# Revit family: vanity unit with 2 drawers
name_source: partatom
category: Furniture
units: mm (PartAtom-declared; Revit-internal decimal feet)

## family parameters
Always vertical = Yes
Cut with Voids When Loaded = No
OmniClass Number = 23.21.19.15.33.13
Room Calculation Point = No
Shared = Yes
Work Plane-Based = No

## types (120) — shared parameters
BIMOBJECT = Sanitary: Compound units
CATALOG = Hansgrohe
DESIGN = Germany
ETIM = EC011381 | Bathroom furniture set
IFC = Furnishing element
MASTERFORMAT = 12 35 30.23 | Bathroom Casework
Manufacturer = Hansgrohe
NBSYN = $BASENUMBER.-$ARTNR.-$OBERFLAECHE.-$SURFACE.-$LODLEVEL.
NN = Vanity Unit with 2 Drawers
OBJECTTYPE = Object (single object)
OMNICLASS = 23-21 19 15 33 13 | Residential Bathroom Specialty Casework
PRODUCTFAMILY = Xelu Q
PRODUCTGROUP = vanity unit
PRODUCTURL = https://pro.hansgrohe.com
REGIONSET = Worldwide
UNICLASS2015 = Pr_40_30_78_05 | Bathroom furniture
UNICLASS_2015_CODE = 40_30_78_05
UNIFORMATII = E2010 | Fixed Furnishings
UNSPSC = 56 | Furniture and Furnishings
etim7_EC011381 = EC011381

## per-type parameters (varying)
| type | ARTNR | BASENUMBER | GTINCODE | L | LINA | LODLEVEL | Model | NAME | NB | OBERFLAECHE | PERMALINK | SURFACE | WEIGHT |
| Vanity unit 1180_475 with 2 drawers for washbasin-54035000-High Gloss White-CHROME-200 | 54035000 | Vanity unit 1180/475 with 2 drawers for washbasin | 4059625455807 | 1180 | Vanity unit 1180/475 with 2 drawers for washbasin-54035000-High Gloss White-CHROME-200 | 200 | Vanity unit 1180/475 with 2 drawers for washbasin-54035000-High Gloss White-CHROME-200 | Xelu Q Vanity unit High Gloss White 1180/475 with 2 drawers for washbasin | Vanity unit 1180/475 with 2 drawers for washbasin-54035000-High Gloss White-CHROME-200 | High Gloss White | 54035XXX | CHROME | 45.5 |
| Vanity unit 1180_475 with 2 drawers for washbasin-54035000-High Gloss White-CHROME-400 | 54035000 | Vanity unit 1180/475 with 2 drawers for washbasin | 4059625455807 | 1180 | Vanity unit 1180/475 with 2 drawers for washbasin-54035000-High Gloss White-CHROME-400 | 400 | Vanity unit 1180/475 with 2 drawers for washbasin-54035000-High Gloss White-CHROME-400 | Xelu Q Vanity unit High Gloss White 1180/475 with 2 drawers for washbasin | Vanity unit 1180/475 with 2 drawers for washbasin-54035000-High Gloss White-CHROME-400 | High Gloss White | 54035XXX | CHROME | 45.5 |
| Vanity unit 1180_475 with 2 drawers for washbasin-54035670-High Gloss White-MATT_BLACK-200 | 54035670 | Vanity unit 1180/475 with 2 drawers for washbasin | 4059625455807 | 1180 | Vanity unit 1180/475 with 2 drawers for washbasin-54035670-High Gloss White-MATT_BLACK-200 | 200 | Vanity unit 1180/475 with 2 drawers for washbasin-54035670-High Gloss White-MATT_BLACK-200 | Xelu Q Vanity unit High Gloss White 1180/475 with 2 drawers for washbasin | Vanity unit 1180/475 with 2 drawers for washbasin-54035670-High Gloss White-MATT_BLACK-200 | High Gloss White | 54035XXX | MATT_BLACK | 45.5 |
| Vanity unit 1180_475 with 2 drawers for washbasin-54035670-High Gloss White-MATT_BLACK-400 | 54035670 | Vanity unit 1180/475 with 2 drawers for washbasin | 4059625455807 | 1180 | Vanity unit 1180/475 with 2 drawers for washbasin-54035670-High Gloss White-MATT_BLACK-400 | 400 | Vanity unit 1180/475 with 2 drawers for washbasin-54035670-High Gloss White-MATT_BLACK-400 | Xelu Q Vanity unit High Gloss White 1180/475 with 2 drawers for washbasin | Vanity unit 1180/475 with 2 drawers for washbasin-54035670-High Gloss White-MATT_BLACK-400 | High Gloss White | 54035XXX | MATT_BLACK | 45.5 |
| Vanity unit 1180_475 with 2 drawers for washbasin-54035700-High Gloss White-MATT_WHITE-200 | 54035700 | Vanity unit 1180/475 with 2 drawers for washbasin | 4059625455807 | 1180 | Vanity unit 1180/475 with 2 drawers for washbasin-54035700-High Gloss White-MATT_WHITE-200 | 200 | Vanity unit 1180/475 with 2 drawers for washbasin-54035700-High Gloss White-MATT_WHITE-200 | Xelu Q Vanity unit High Gloss White 1180/475 with 2 drawers for washbasin | Vanity unit 1180/475 with 2 drawers for washbasin-54035700-High Gloss White-MATT_WHITE-200 | High Gloss White | 54035XXX | MATT_WHITE | 45.5 |
| Vanity unit 1180_475 with 2 drawers for washbasin-54035700-High Gloss White-MATT_WHITE-400 | 54035700 | Vanity unit 1180/475 with 2 drawers for washbasin | 4059625455807 | 1180 | Vanity unit 1180/475 with 2 drawers for washbasin-54035700-High Gloss White-MATT_WHITE-400 | 400 | Vanity unit 1180/475 with 2 drawers for washbasin-54035700-High Gloss White-MATT_WHITE-400 | Xelu Q Vanity unit High Gloss White 1180/475 with 2 drawers for washbasin | Vanity unit 1180/475 with 2 drawers for washbasin-54035700-High Gloss White-MATT_WHITE-400 | High Gloss White | 54035XXX | MATT_WHITE | 45.5 |
| Vanity unit 1180_475 with 2 drawers for washbasin-54036000-Diamond Matt Grey-CHROME-200 | 54036000 | Vanity unit 1180/475 with 2 drawers for washbasin | 4059625455777 | 1180 | Vanity unit 1180/475 with 2 drawers for washbasin-54036000-Diamond Matt Grey-CHROME-200 | 200 | Vanity unit 1180/475 with 2 drawers for washbasin-54036000-Diamond Matt Grey-CHROME-200 | Xelu Q Vanity unit Diamond Matt Grey 1180/475 with 2 drawers for washbasin | Vanity unit 1180/475 with 2 drawers for washbasin-54036000-Diamond Matt Grey-CHROME-200 | Diamond Matt Grey | 54036XXX | CHROME | 45.5 |
| Vanity unit 1180_475 with 2 drawers for washbasin-54036000-Diamond Matt Grey-CHROME-400 | 54036000 | Vanity unit 1180/475 with 2 drawers for washbasin | 4059625455777 | 1180 | Vanity unit 1180/475 with 2 drawers for washbasin-54036000-Diamond Matt Grey-CHROME-400 | 400 | Vanity unit 1180/475 with 2 drawers for washbasin-54036000-Diamond Matt Grey-CHROME-400 | Xelu Q Vanity unit Diamond Matt Grey 1180/475 with 2 drawers for washbasin | Vanity unit 1180/475 with 2 drawers for washbasin-54036000-Diamond Matt Grey-CHROME-400 | Diamond Matt Grey | 54036XXX | CHROME | 45.5 |
| Vanity unit 1180_475 with 2 drawers for washbasin-54036670-Diamond Matt Grey-MATT_BLACK-200 | 54036670 | Vanity unit 1180/475 with 2 drawers for washbasin | 4059625455777 | 1180 | Vanity unit 1180/475 with 2 drawers for washbasin-54036670-Diamond Matt Grey-MATT_BLACK-200 | 200 | Vanity unit 1180/475 with 2 drawers for washbasin-54036670-Diamond Matt Grey-MATT_BLACK-200 | Xelu Q Vanity unit Diamond Matt Grey 1180/475 with 2 drawers for washbasin | Vanity unit 1180/475 with 2 drawers for washbasin-54036670-Diamond Matt Grey-MATT_BLACK-200 | Diamond Matt Grey | 54036XXX | MATT_BLACK | 45.5 |
| Vanity unit 1180_475 with 2 drawers for washbasin-54036670-Diamond Matt Grey-MATT_BLACK-400 | 54036670 | Vanity unit 1180/475 with 2 drawers for washbasin | 4059625455777 | 1180 | Vanity unit 1180/475 with 2 drawers for washbasin-54036670-Diamond Matt Grey-MATT_BLACK-400 | 400 | Vanity unit 1180/475 with 2 drawers for washbasin-54036670-Diamond Matt Grey-MATT_BLACK-400 | Xelu Q Vanity unit Diamond Matt Grey 1180/475 with 2 drawers for washbasin | Vanity unit 1180/475 with 2 drawers for washbasin-54036670-Diamond Matt Grey-MATT_BLACK-400 | Diamond Matt Grey | 54036XXX | MATT_BLACK | 45.5 |
| Vanity unit 1180_475 with 2 drawers for washbasin-54036700-Diamond Matt Grey-MATT_WHITE-200 | 54036700 | Vanity unit 1180/475 with 2 drawers for washbasin | 4059625455777 | 1180 | Vanity unit 1180/475 with 2 drawers for washbasin-54036700-Diamond Matt Grey-MATT_WHITE-200 | 200 | Vanity unit 1180/475 with 2 drawers for washbasin-54036700-Diamond Matt Grey-MATT_WHITE-200 | Xelu Q Vanity unit Diamond Matt Grey 1180/475 with 2 drawers for washbasin | Vanity unit 1180/475 with 2 drawers for washbasin-54036700-Diamond Matt Grey-MATT_WHITE-200 | Diamond Matt Grey | 54036XXX | MATT_WHITE | 45.5 |
| Vanity unit 1180_475 with 2 drawers for washbasin-54036700-Diamond Matt Grey-MATT_WHITE-400 | 54036700 | Vanity unit 1180/475 with 2 drawers for washbasin | 4059625455777 | 1180 | Vanity unit 1180/475 with 2 drawers for washbasin-54036700-Diamond Matt Grey-MATT_WHITE-400 | 400 | Vanity unit 1180/475 with 2 drawers for washbasin-54036700-Diamond Matt Grey-MATT_WHITE-400 | Xelu Q Vanity unit Diamond Matt Grey 1180/475 with 2 drawers for washbasin | Vanity unit 1180/475 with 2 drawers for washbasin-54036700-Diamond Matt Grey-MATT_WHITE-400 | Diamond Matt Grey | 54036XXX | MATT_WHITE | 45.5 |
| Vanity unit 1180_475 with 2 drawers for washbasin-54037000-Natural Oak-CHROME-200 | 54037000 | Vanity unit 1180/475 with 2 drawers for washbasin | 4059625455746 | 1180 | Vanity unit 1180/475 with 2 drawers for washbasin-54037000-Natural Oak-CHROME-200 | 200 | Vanity unit 1180/475 with 2 drawers for washbasin-54037000-Natural Oak-CHROME-200 | Xelu Q Vanity unit Natural Oak 1180/475 with 2 drawers for washbasin | Vanity unit 1180/475 with 2 drawers for washbasin-54037000-Natural Oak-CHROME-200 | Natural Oak | 54037XXX | CHROME | 45.5 |
| Vanity unit 1180_475 with 2 drawers for washbasin-54037000-Natural Oak-CHROME-400 | 54037000 | Vanity unit 1180/475 with 2 drawers for washbasin | 4059625455746 | 1180 | Vanity unit 1180/475 with 2 drawers for washbasin-54037000-Natural Oak-CHROME-400 | 400 | Vanity unit 1180/475 with 2 drawers for washbasin-54037000-Natural Oak-CHROME-400 | Xelu Q Vanity unit Natural Oak 1180/475 with 2 drawers for washbasin | Vanity unit 1180/475 with 2 drawers for washbasin-54037000-Natural Oak-CHROME-400 | Natural Oak | 54037XXX | CHROME | 45.5 |
| Vanity unit 1180_475 with 2 drawers for washbasin-54037670-Natural Oak-MATT_BLACK-200 | 54037670 | Vanity unit 1180/475 with 2 drawers for washbasin | 4059625455746 | 1180 | Vanity unit 1180/475 with 2 drawers for washbasin-54037670-Natural Oak-MATT_BLACK-200 | 200 | Vanity unit 1180/475 with 2 drawers for washbasin-54037670-Natural Oak-MATT_BLACK-200 | Xelu Q Vanity unit Natural Oak 1180/475 with 2 drawers for washbasin | Vanity unit 1180/475 with 2 drawers for washbasin-54037670-Natural Oak-MATT_BLACK-200 | Natural Oak | 54037XXX | MATT_BLACK | 45.5 |
| Vanity unit 1180_475 with 2 drawers for washbasin-54037670-Natural Oak-MATT_BLACK-400 | 54037670 | Vanity unit 1180/475 with 2 drawers for washbasin | 4059625455746 | 1180 | Vanity unit 1180/475 with 2 drawers for washbasin-54037670-Natural Oak-MATT_BLACK-400 | 400 | Vanity unit 1180/475 with 2 drawers for washbasin-54037670-Natural Oak-MATT_BLACK-400 | Xelu Q Vanity unit Natural Oak 1180/475 with 2 drawers for washbasin | Vanity unit 1180/475 with 2 drawers for washbasin-54037670-Natural Oak-MATT_BLACK-400 | Natural Oak | 54037XXX | MATT_BLACK | 45.5 |
| Vanity unit 1180_475 with 2 drawers for washbasin-54037700-Natural Oak-MATT_WHITE-200 | 54037700 | Vanity unit 1180/475 with 2 drawers for washbasin | 4059625455746 | 1180 | Vanity unit 1180/475 with 2 drawers for washbasin-54037700-Natural Oak-MATT_WHITE-200 | 200 | Vanity unit 1180/475 with 2 drawers for washbasin-54037700-Natural Oak-MATT_WHITE-200 | Xelu Q Vanity unit Natural Oak 1180/475 with 2 drawers for washbasin | Vanity unit 1180/475 with 2 drawers for washbasin-54037700-Natural Oak-MATT_WHITE-200 | Natural Oak | 54037XXX | MATT_WHITE | 45.5 |
| Vanity unit 1180_475 with 2 drawers for washbasin-54037700-Natural Oak-MATT_WHITE-400 | 54037700 | Vanity unit 1180/475 with 2 drawers for washbasin | 4059625455746 | 1180 | Vanity unit 1180/475 with 2 drawers for washbasin-54037700-Natural Oak-MATT_WHITE-400 | 400 | Vanity unit 1180/475 with 2 drawers for washbasin-54037700-Natural Oak-MATT_WHITE-400 | Xelu Q Vanity unit Natural Oak 1180/475 with 2 drawers for washbasin | Vanity unit 1180/475 with 2 drawers for washbasin-54037700-Natural Oak-MATT_WHITE-400 | Natural Oak | 54037XXX | MATT_WHITE | 45.5 |
| Vanity unit 1180_475 with 2 drawers for washbasin-54038000-Dark Walnut-CHROME-200 | 54038000 | Vanity unit 1180/475 with 2 drawers for washbasin | 4059625455715 | 1180 | Vanity unit 1180/475 with 2 drawers for washbasin-54038000-Dark Walnut-CHROME-200 | 200 | Vanity unit 1180/475 with 2 drawers for washbasin-54038000-Dark Walnut-CHROME-200 | Xelu Q Vanity unit Dark Walnut 1180/475 with 2 drawers for washbasin | Vanity unit 1180/475 with 2 drawers for washbasin-54038000-Dark Walnut-CHROME-200 | Dark Walnut | 54038XXX | CHROME | 45.5 |
| Vanity unit 1180_475 with 2 drawers for washbasin-54038000-Dark Walnut-CHROME-400 | 54038000 | Vanity unit 1180/475 with 2 drawers for washbasin | 4059625455715 | 1180 | Vanity unit 1180/475 with 2 drawers for washbasin-54038000-Dark Walnut-CHROME-400 | 400 | Vanity unit 1180/475 with 2 drawers for washbasin-54038000-Dark Walnut-CHROME-400 | Xelu Q Vanity unit Dark Walnut 1180/475 with 2 drawers for washbasin | Vanity unit 1180/475 with 2 drawers for washbasin-54038000-Dark Walnut-CHROME-400 | Dark Walnut | 54038XXX | CHROME | 45.5 |
| Vanity unit 1180_475 with 2 drawers for washbasin-54038670-Dark Walnut-MATT_BLACK-200 | 54038670 | Vanity unit 1180/475 with 2 drawers for washbasin | 4059625455715 | 1180 | Vanity unit 1180/475 with 2 drawers for washbasin-54038670-Dark Walnut-MATT_BLACK-200 | 200 | Vanity unit 1180/475 with 2 drawers for washbasin-54038670-Dark Walnut-MATT_BLACK-200 | Xelu Q Vanity unit Dark Walnut 1180/475 with 2 drawers for washbasin | Vanity unit 1180/475 with 2 drawers for washbasin-54038670-Dark Walnut-MATT_BLACK-200 | Dark Walnut | 54038XXX | MATT_BLACK | 45.5 |
| Vanity unit 1180_475 with 2 drawers for washbasin-54038670-Dark Walnut-MATT_BLACK-400 | 54038670 | Vanity unit 1180/475 with 2 drawers for washbasin | 4059625455715 | 1180 | Vanity unit 1180/475 with 2 drawers for washbasin-54038670-Dark Walnut-MATT_BLACK-400 | 400 | Vanity unit 1180/475 with 2 drawers for washbasin-54038670-Dark Walnut-MATT_BLACK-400 | Xelu Q Vanity unit Dark Walnut 1180/475 with 2 drawers for washbasin | Vanity unit 1180/475 with 2 drawers for washbasin-54038670-Dark Walnut-MATT_BLACK-400 | Dark Walnut | 54038XXX | MATT_BLACK | 45.5 |
| Vanity unit 1180_475 with 2 drawers for washbasin-54038700-Dark Walnut-MATT_WHITE-200 | 54038700 | Vanity unit 1180/475 with 2 drawers for washbasin | 4059625455715 | 1180 | Vanity unit 1180/475 with 2 drawers for washbasin-54038700-Dark Walnut-MATT_WHITE-200 | 200 | Vanity unit 1180/475 with 2 drawers for washbasin-54038700-Dark Walnut-MATT_WHITE-200 | Xelu Q Vanity unit Dark Walnut 1180/475 with 2 drawers for washbasin | Vanity unit 1180/475 with 2 drawers for washbasin-54038700-Dark Walnut-MATT_WHITE-200 | Dark Walnut | 54038XXX | MATT_WHITE | 45.5 |
| Vanity unit 1180_475 with 2 drawers for washbasin-54038700-Dark Walnut-MATT_WHITE-400 | 54038700 | Vanity unit 1180/475 with 2 drawers for washbasin | 4059625455715 | 1180 | Vanity unit 1180/475 with 2 drawers for washbasin-54038700-Dark Walnut-MATT_WHITE-400 | 400 | Vanity unit 1180/475 with 2 drawers for washbasin-54038700-Dark Walnut-MATT_WHITE-400 | Xelu Q Vanity unit Dark Walnut 1180/475 with 2 drawers for washbasin | Vanity unit 1180/475 with 2 drawers for washbasin-54038700-Dark Walnut-MATT_WHITE-400 | Dark Walnut | 54038XXX | MATT_WHITE | 45.5 |
| Vanity unit 480_475 with 2 drawers for handrinse basin-54019000-High Gloss White-CHROME-200 | 54019000 | Vanity unit 480/475 with 2 drawers for handrinse basin | 4059625455289 | 480 | Vanity unit 480/475 with 2 drawers for handrinse basin-54019000-High Gloss White-CHROME-200 | 200 | Vanity unit 480/475 with 2 drawers for handrinse basin-54019000-High Gloss White-CHROME-200 | Xelu Q Vanity unit High Gloss White 480/475 with 2 drawers for handrinse basin | Vanity unit 480/475 with 2 drawers for handrinse basin-54019000-High Gloss White-CHROME-200 | High Gloss White | 54019XXX | CHROME | 25.3 |
| Vanity unit 480_475 with 2 drawers for handrinse basin-54019000-High Gloss White-CHROME-400 | 54019000 | Vanity unit 480/475 with 2 drawers for handrinse basin | 4059625455289 | 480 | Vanity unit 480/475 with 2 drawers for handrinse basin-54019000-High Gloss White-CHROME-400 | 400 | Vanity unit 480/475 with 2 drawers for handrinse basin-54019000-High Gloss White-CHROME-400 | Xelu Q Vanity unit High Gloss White 480/475 with 2 drawers for handrinse basin | Vanity unit 480/475 with 2 drawers for handrinse basin-54019000-High Gloss White-CHROME-400 | High Gloss White | 54019XXX | CHROME | 25.3 |
| Vanity unit 480_475 with 2 drawers for handrinse basin-54019670-High Gloss White-MATT_BLACK-200 | 54019670 | Vanity unit 480/475 with 2 drawers for handrinse basin | 4059625455289 | 480 | Vanity unit 480/475 with 2 drawers for handrinse basin-54019670-High Gloss White-MATT_BLACK-200 | 200 | Vanity unit 480/475 with 2 drawers for handrinse basin-54019670-High Gloss White-MATT_BLACK-200 | Xelu Q Vanity unit High Gloss White 480/475 with 2 drawers for handrinse basin | Vanity unit 480/475 with 2 drawers for handrinse basin-54019670-High Gloss White-MATT_BLACK-200 | High Gloss White | 54019XXX | MATT_BLACK | 25.3 |
| Vanity unit 480_475 with 2 drawers for handrinse basin-54019670-High Gloss White-MATT_BLACK-400 | 54019670 | Vanity unit 480/475 with 2 drawers for handrinse basin | 4059625455289 | 480 | Vanity unit 480/475 with 2 drawers for handrinse basin-54019670-High Gloss White-MATT_BLACK-400 | 400 | Vanity unit 480/475 with 2 drawers for handrinse basin-54019670-High Gloss White-MATT_BLACK-400 | Xelu Q Vanity unit High Gloss White 480/475 with 2 drawers for handrinse basin | Vanity unit 480/475 with 2 drawers for handrinse basin-54019670-High Gloss White-MATT_BLACK-400 | High Gloss White | 54019XXX | MATT_BLACK | 25.3 |
| Vanity unit 480_475 with 2 drawers for handrinse basin-54019700-High Gloss White-MATT_WHITE-200 | 54019700 | Vanity unit 480/475 with 2 drawers for handrinse basin | 4059625455289 | 480 | Vanity unit 480/475 with 2 drawers for handrinse basin-54019700-High Gloss White-MATT_WHITE-200 | 200 | Vanity unit 480/475 with 2 drawers for handrinse basin-54019700-High Gloss White-MATT_WHITE-200 | Xelu Q Vanity unit High Gloss White 480/475 with 2 drawers for handrinse basin | Vanity unit 480/475 with 2 drawers for handrinse basin-54019700-High Gloss White-MATT_WHITE-200 | High Gloss White | 54019XXX | MATT_WHITE | 25.3 |
| Vanity unit 480_475 with 2 drawers for handrinse basin-54019700-High Gloss White-MATT_WHITE-400 | 54019700 | Vanity unit 480/475 with 2 drawers for handrinse basin | 4059625455289 | 480 | Vanity unit 480/475 with 2 drawers for handrinse basin-54019700-High Gloss White-MATT_WHITE-400 | 400 | Vanity unit 480/475 with 2 drawers for handrinse basin-54019700-High Gloss White-MATT_WHITE-400 | Xelu Q Vanity unit High Gloss White 480/475 with 2 drawers for handrinse basin | Vanity unit 480/475 with 2 drawers for handrinse basin-54019700-High Gloss White-MATT_WHITE-400 | High Gloss White | 54019XXX | MATT_WHITE | 25.3 |
| Vanity unit 480_475 with 2 drawers for handrinse basin-54020000-Diamond Matt Grey-CHROME-200 | 54020000 | Vanity unit 480/475 with 2 drawers for handrinse basin | 4059625455258 | 480 | Vanity unit 480/475 with 2 drawers for handrinse basin-54020000-Diamond Matt Grey-CHROME-200 | 200 | Vanity unit 480/475 with 2 drawers for handrinse basin-54020000-Diamond Matt Grey-CHROME-200 | Xelu Q Vanity unit Diamond Matt Grey 480/475 with 2 drawers for handrinse basin | Vanity unit 480/475 with 2 drawers for handrinse basin-54020000-Diamond Matt Grey-CHROME-200 | Diamond Matt Grey | 54020XXX | CHROME | 25.3 |
| Vanity unit 480_475 with 2 drawers for handrinse basin-54020000-Diamond Matt Grey-CHROME-400 | 54020000 | Vanity unit 480/475 with 2 drawers for handrinse basin | 4059625455258 | 480 | Vanity unit 480/475 with 2 drawers for handrinse basin-54020000-Diamond Matt Grey-CHROME-400 | 400 | Vanity unit 480/475 with 2 drawers for handrinse basin-54020000-Diamond Matt Grey-CHROME-400 | Xelu Q Vanity unit Diamond Matt Grey 480/475 with 2 drawers for handrinse basin | Vanity unit 480/475 with 2 drawers for handrinse basin-54020000-Diamond Matt Grey-CHROME-400 | Diamond Matt Grey | 54020XXX | CHROME | 25.3 |
| Vanity unit 480_475 with 2 drawers for handrinse basin-54020670-Diamond Matt Grey-MATT_BLACK-200 | 54020670 | Vanity unit 480/475 with 2 drawers for handrinse basin | 4059625455258 | 480 | Vanity unit 480/475 with 2 drawers for handrinse basin-54020670-Diamond Matt Grey-MATT_BLACK-200 | 200 | Vanity unit 480/475 with 2 drawers for handrinse basin-54020670-Diamond Matt Grey-MATT_BLACK-200 | Xelu Q Vanity unit Diamond Matt Grey 480/475 with 2 drawers for handrinse basin | Vanity unit 480/475 with 2 drawers for handrinse basin-54020670-Diamond Matt Grey-MATT_BLACK-200 | Diamond Matt Grey | 54020XXX | MATT_BLACK | 25.3 |
| Vanity unit 480_475 with 2 drawers for handrinse basin-54020670-Diamond Matt Grey-MATT_BLACK-400 | 54020670 | Vanity unit 480/475 with 2 drawers for handrinse basin | 4059625455258 | 480 | Vanity unit 480/475 with 2 drawers for handrinse basin-54020670-Diamond Matt Grey-MATT_BLACK-400 | 400 | Vanity unit 480/475 with 2 drawers for handrinse basin-54020670-Diamond Matt Grey-MATT_BLACK-400 | Xelu Q Vanity unit Diamond Matt Grey 480/475 with 2 drawers for handrinse basin | Vanity unit 480/475 with 2 drawers for handrinse basin-54020670-Diamond Matt Grey-MATT_BLACK-400 | Diamond Matt Grey | 54020XXX | MATT_BLACK | 25.3 |
| Vanity unit 480_475 with 2 drawers for handrinse basin-54020700-Diamond Matt Grey-MATT_WHITE-200 | 54020700 | Vanity unit 480/475 with 2 drawers for handrinse basin | 4059625455258 | 480 | Vanity unit 480/475 with 2 drawers for handrinse basin-54020700-Diamond Matt Grey-MATT_WHITE-200 | 200 | Vanity unit 480/475 with 2 drawers for handrinse basin-54020700-Diamond Matt Grey-MATT_WHITE-200 | Xelu Q Vanity unit Diamond Matt Grey 480/475 with 2 drawers for handrinse basin | Vanity unit 480/475 with 2 drawers for handrinse basin-54020700-Diamond Matt Grey-MATT_WHITE-200 | Diamond Matt Grey | 54020XXX | MATT_WHITE | 25.3 |
| Vanity unit 480_475 with 2 drawers for handrinse basin-54020700-Diamond Matt Grey-MATT_WHITE-400 | 54020700 | Vanity unit 480/475 with 2 drawers for handrinse basin | 4059625455258 | 480 | Vanity unit 480/475 with 2 drawers for handrinse basin-54020700-Diamond Matt Grey-MATT_WHITE-400 | 400 | Vanity unit 480/475 with 2 drawers for handrinse basin-54020700-Diamond Matt Grey-MATT_WHITE-400 | Xelu Q Vanity unit Diamond Matt Grey 480/475 with 2 drawers for handrinse basin | Vanity unit 480/475 with 2 drawers for handrinse basin-54020700-Diamond Matt Grey-MATT_WHITE-400 | Diamond Matt Grey | 54020XXX | MATT_WHITE | 25.3 |
| Vanity unit 480_475 with 2 drawers for handrinse basin-54021000-Natural Oak-CHROME-200 | 54021000 | Vanity unit 480/475 with 2 drawers for handrinse basin | 4059625455227 | 480 | Vanity unit 480/475 with 2 drawers for handrinse basin-54021000-Natural Oak-CHROME-200 | 200 | Vanity unit 480/475 with 2 drawers for handrinse basin-54021000-Natural Oak-CHROME-200 | Xelu Q Vanity unit Natural Oak 480/475 with 2 drawers for handrinse basin | Vanity unit 480/475 with 2 drawers for handrinse basin-54021000-Natural Oak-CHROME-200 | Natural Oak | 54021XXX | CHROME | 25.3 |
| Vanity unit 480_475 with 2 drawers for handrinse basin-54021000-Natural Oak-CHROME-400 | 54021000 | Vanity unit 480/475 with 2 drawers for handrinse basin | 4059625455227 | 480 | Vanity unit 480/475 with 2 drawers for handrinse basin-54021000-Natural Oak-CHROME-400 | 400 | Vanity unit 480/475 with 2 drawers for handrinse basin-54021000-Natural Oak-CHROME-400 | Xelu Q Vanity unit Natural Oak 480/475 with 2 drawers for handrinse basin | Vanity unit 480/475 with 2 drawers for handrinse basin-54021000-Natural Oak-CHROME-400 | Natural Oak | 54021XXX | CHROME | 25.3 |
| Vanity unit 480_475 with 2 drawers for handrinse basin-54021670-Natural Oak-MATT_BLACK-200 | 54021670 | Vanity unit 480/475 with 2 drawers for handrinse basin | 4059625455227 | 480 | Vanity unit 480/475 with 2 drawers for handrinse basin-54021670-Natural Oak-MATT_BLACK-200 | 200 | Vanity unit 480/475 with 2 drawers for handrinse basin-54021670-Natural Oak-MATT_BLACK-200 | Xelu Q Vanity unit Natural Oak 480/475 with 2 drawers for handrinse basin | Vanity unit 480/475 with 2 drawers for handrinse basin-54021670-Natural Oak-MATT_BLACK-200 | Natural Oak | 54021XXX | MATT_BLACK | 25.3 |
| Vanity unit 480_475 with 2 drawers for handrinse basin-54021670-Natural Oak-MATT_BLACK-400 | 54021670 | Vanity unit 480/475 with 2 drawers for handrinse basin | 4059625455227 | 480 | Vanity unit 480/475 with 2 drawers for handrinse basin-54021670-Natural Oak-MATT_BLACK-400 | 400 | Vanity unit 480/475 with 2 drawers for handrinse basin-54021670-Natural Oak-MATT_BLACK-400 | Xelu Q Vanity unit Natural Oak 480/475 with 2 drawers for handrinse basin | Vanity unit 480/475 with 2 drawers for handrinse basin-54021670-Natural Oak-MATT_BLACK-400 | Natural Oak | 54021XXX | MATT_BLACK | 25.3 |
| Vanity unit 480_475 with 2 drawers for handrinse basin-54021700-Natural Oak-MATT_WHITE-200 | 54021700 | Vanity unit 480/475 with 2 drawers for handrinse basin | 4059625455227 | 480 | Vanity unit 480/475 with 2 drawers for handrinse basin-54021700-Natural Oak-MATT_WHITE-200 | 200 | Vanity unit 480/475 with 2 drawers for handrinse basin-54021700-Natural Oak-MATT_WHITE-200 | Xelu Q Vanity unit Natural Oak 480/475 with 2 drawers for handrinse basin | Vanity unit 480/475 with 2 drawers for handrinse basin-54021700-Natural Oak-MATT_WHITE-200 | Natural Oak | 54021XXX | MATT_WHITE | 25.3 |
| Vanity unit 480_475 with 2 drawers for handrinse basin-54021700-Natural Oak-MATT_WHITE-400 | 54021700 | Vanity unit 480/475 with 2 drawers for handrinse basin | 4059625455227 | 480 | Vanity unit 480/475 with 2 drawers for handrinse basin-54021700-Natural Oak-MATT_WHITE-400 | 400 | Vanity unit 480/475 with 2 drawers for handrinse basin-54021700-Natural Oak-MATT_WHITE-400 | Xelu Q Vanity unit Natural Oak 480/475 with 2 drawers for handrinse basin | Vanity unit 480/475 with 2 drawers for handrinse basin-54021700-Natural Oak-MATT_WHITE-400 | Natural Oak | 54021XXX | MATT_WHITE | 25.3 |
| Vanity unit 480_475 with 2 drawers for handrinse basin-54022000-Dark Walnut-CHROME-200 | 54022000 | Vanity unit 480/475 with 2 drawers for handrinse basin | 4059625455197 | 480 | Vanity unit 480/475 with 2 drawers for handrinse basin-54022000-Dark Walnut-CHROME-200 | 200 | Vanity unit 480/475 with 2 drawers for handrinse basin-54022000-Dark Walnut-CHROME-200 | Xelu Q Vanity unit Dark Walnut 480/475 with 2 drawers for handrinse basin | Vanity unit 480/475 with 2 drawers for handrinse basin-54022000-Dark Walnut-CHROME-200 | Dark Walnut | 54022XXX | CHROME | 25.3 |
| Vanity unit 480_475 with 2 drawers for handrinse basin-54022000-Dark Walnut-CHROME-400 | 54022000 | Vanity unit 480/475 with 2 drawers for handrinse basin | 4059625455197 | 480 | Vanity unit 480/475 with 2 drawers for handrinse basin-54022000-Dark Walnut-CHROME-400 | 400 | Vanity unit 480/475 with 2 drawers for handrinse basin-54022000-Dark Walnut-CHROME-400 | Xelu Q Vanity unit Dark Walnut 480/475 with 2 drawers for handrinse basin | Vanity unit 480/475 with 2 drawers for handrinse basin-54022000-Dark Walnut-CHROME-400 | Dark Walnut | 54022XXX | CHROME | 25.3 |
| Vanity unit 480_475 with 2 drawers for handrinse basin-54022670-Dark Walnut-MATT_BLACK-200 | 54022670 | Vanity unit 480/475 with 2 drawers for handrinse basin | 4059625455197 | 480 | Vanity unit 480/475 with 2 drawers for handrinse basin-54022670-Dark Walnut-MATT_BLACK-200 | 200 | Vanity unit 480/475 with 2 drawers for handrinse basin-54022670-Dark Walnut-MATT_BLACK-200 | Xelu Q Vanity unit Dark Walnut 480/475 with 2 drawers for handrinse basin | Vanity unit 480/475 with 2 drawers for handrinse basin-54022670-Dark Walnut-MATT_BLACK-200 | Dark Walnut | 54022XXX | MATT_BLACK | 25.3 |
| Vanity unit 480_475 with 2 drawers for handrinse basin-54022670-Dark Walnut-MATT_BLACK-400 | 54022670 | Vanity unit 480/475 with 2 drawers for handrinse basin | 4059625455197 | 480 | Vanity unit 480/475 with 2 drawers for handrinse basin-54022670-Dark Walnut-MATT_BLACK-400 | 400 | Vanity unit 480/475 with 2 drawers for handrinse basin-54022670-Dark Walnut-MATT_BLACK-400 | Xelu Q Vanity unit Dark Walnut 480/475 with 2 drawers for handrinse basin | Vanity unit 480/475 with 2 drawers for handrinse basin-54022670-Dark Walnut-MATT_BLACK-400 | Dark Walnut | 54022XXX | MATT_BLACK | 25.3 |
| Vanity unit 480_475 with 2 drawers for handrinse basin-54022700-Dark Walnut-MATT_WHITE-200 | 54022700 | Vanity unit 480/475 with 2 drawers for handrinse basin | 4059625455197 | 480 | Vanity unit 480/475 with 2 drawers for handrinse basin-54022700-Dark Walnut-MATT_WHITE-200 | 200 | Vanity unit 480/475 with 2 drawers for handrinse basin-54022700-Dark Walnut-MATT_WHITE-200 | Xelu Q Vanity unit Dark Walnut 480/475 with 2 drawers for handrinse basin | Vanity unit 480/475 with 2 drawers for handrinse basin-54022700-Dark Walnut-MATT_WHITE-200 | Dark Walnut | 54022XXX | MATT_WHITE | 25.3 |
| Vanity unit 480_475 with 2 drawers for handrinse basin-54022700-Dark Walnut-MATT_WHITE-400 | 54022700 | Vanity unit 480/475 with 2 drawers for handrinse basin | 4059625455197 | 480 | Vanity unit 480/475 with 2 drawers for handrinse basin-54022700-Dark Walnut-MATT_WHITE-400 | 400 | Vanity unit 480/475 with 2 drawers for handrinse basin-54022700-Dark Walnut-MATT_WHITE-400 | Xelu Q Vanity unit Dark Walnut 480/475 with 2 drawers for handrinse basin | Vanity unit 480/475 with 2 drawers for handrinse basin-54022700-Dark Walnut-MATT_WHITE-400 | Dark Walnut | 54022XXX | MATT_WHITE | 25.3 |
| Vanity unit 580_475 with 2 drawers for washbasin-54023000-High Gloss White-CHROME-200 | 54023000 | Vanity unit 580/475 with 2 drawers for washbasin | 4059625455166 | 580 | Vanity unit 580/475 with 2 drawers for washbasin-54023000-High Gloss White-CHROME-200 | 200 | Vanity unit 580/475 with 2 drawers for washbasin-54023000-High Gloss White-CHROME-200 | Xelu Q Vanity unit High Gloss White 580/475 with 2 drawers for washbasin | Vanity unit 580/475 with 2 drawers for washbasin-54023000-High Gloss White-CHROME-200 | High Gloss White | 54023XXX | CHROME | 28.2 |
| Vanity unit 580_475 with 2 drawers for washbasin-54023000-High Gloss White-CHROME-400 | 54023000 | Vanity unit 580/475 with 2 drawers for washbasin | 4059625455166 | 580 | Vanity unit 580/475 with 2 drawers for washbasin-54023000-High Gloss White-CHROME-400 | 400 | Vanity unit 580/475 with 2 drawers for washbasin-54023000-High Gloss White-CHROME-400 | Xelu Q Vanity unit High Gloss White 580/475 with 2 drawers for washbasin | Vanity unit 580/475 with 2 drawers for washbasin-54023000-High Gloss White-CHROME-400 | High Gloss White | 54023XXX | CHROME | 28.2 |
| Vanity unit 580_475 with 2 drawers for washbasin-54023670-High Gloss White-MATT_BLACK-200 | 54023670 | Vanity unit 580/475 with 2 drawers for washbasin | 4059625455166 | 580 | Vanity unit 580/475 with 2 drawers for washbasin-54023670-High Gloss White-MATT_BLACK-200 | 200 | Vanity unit 580/475 with 2 drawers for washbasin-54023670-High Gloss White-MATT_BLACK-200 | Xelu Q Vanity unit High Gloss White 580/475 with 2 drawers for washbasin | Vanity unit 580/475 with 2 drawers for washbasin-54023670-High Gloss White-MATT_BLACK-200 | High Gloss White | 54023XXX | MATT_BLACK | 28.2 |
| Vanity unit 580_475 with 2 drawers for washbasin-54023670-High Gloss White-MATT_BLACK-400 | 54023670 | Vanity unit 580/475 with 2 drawers for washbasin | 4059625455166 | 580 | Vanity unit 580/475 with 2 drawers for washbasin-54023670-High Gloss White-MATT_BLACK-400 | 400 | Vanity unit 580/475 with 2 drawers for washbasin-54023670-High Gloss White-MATT_BLACK-400 | Xelu Q Vanity unit High Gloss White 580/475 with 2 drawers for washbasin | Vanity unit 580/475 with 2 drawers for washbasin-54023670-High Gloss White-MATT_BLACK-400 | High Gloss White | 54023XXX | MATT_BLACK | 28.2 |
| Vanity unit 580_475 with 2 drawers for washbasin-54023700-High Gloss White-MATT_WHITE-200 | 54023700 | Vanity unit 580/475 with 2 drawers for washbasin | 4059625455166 | 580 | Vanity unit 580/475 with 2 drawers for washbasin-54023700-High Gloss White-MATT_WHITE-200 | 200 | Vanity unit 580/475 with 2 drawers for washbasin-54023700-High Gloss White-MATT_WHITE-200 | Xelu Q Vanity unit High Gloss White 580/475 with 2 drawers for washbasin | Vanity unit 580/475 with 2 drawers for washbasin-54023700-High Gloss White-MATT_WHITE-200 | High Gloss White | 54023XXX | MATT_WHITE | 28.2 |
| Vanity unit 580_475 with 2 drawers for washbasin-54023700-High Gloss White-MATT_WHITE-400 | 54023700 | Vanity unit 580/475 with 2 drawers for washbasin | 4059625455166 | 580 | Vanity unit 580/475 with 2 drawers for washbasin-54023700-High Gloss White-MATT_WHITE-400 | 400 | Vanity unit 580/475 with 2 drawers for washbasin-54023700-High Gloss White-MATT_WHITE-400 | Xelu Q Vanity unit High Gloss White 580/475 with 2 drawers for washbasin | Vanity unit 580/475 with 2 drawers for washbasin-54023700-High Gloss White-MATT_WHITE-400 | High Gloss White | 54023XXX | MATT_WHITE | 28.2 |
| Vanity unit 580_475 with 2 drawers for washbasin-54024000-Diamond Matt Grey-CHROME-200 | 54024000 | Vanity unit 580/475 with 2 drawers for washbasin | 4059625455630 | 580 | Vanity unit 580/475 with 2 drawers for washbasin-54024000-Diamond Matt Grey-CHROME-200 | 200 | Vanity unit 580/475 with 2 drawers for washbasin-54024000-Diamond Matt Grey-CHROME-200 | Xelu Q Vanity unit Diamond Matt Grey 580/475 with 2 drawers for washbasin | Vanity unit 580/475 with 2 drawers for washbasin-54024000-Diamond Matt Grey-CHROME-200 | Diamond Matt Grey | 54024XXX | CHROME | 28.2 |
| Vanity unit 580_475 with 2 drawers for washbasin-54024000-Diamond Matt Grey-CHROME-400 | 54024000 | Vanity unit 580/475 with 2 drawers for washbasin | 4059625455630 | 580 | Vanity unit 580/475 with 2 drawers for washbasin-54024000-Diamond Matt Grey-CHROME-400 | 400 | Vanity unit 580/475 with 2 drawers for washbasin-54024000-Diamond Matt Grey-CHROME-400 | Xelu Q Vanity unit Diamond Matt Grey 580/475 with 2 drawers for washbasin | Vanity unit 580/475 with 2 drawers for washbasin-54024000-Diamond Matt Grey-CHROME-400 | Diamond Matt Grey | 54024XXX | CHROME | 28.2 |
| Vanity unit 580_475 with 2 drawers for washbasin-54024670-Diamond Matt Grey-MATT_BLACK-200 | 54024670 | Vanity unit 580/475 with 2 drawers for washbasin | 4059625455630 | 580 | Vanity unit 580/475 with 2 drawers for washbasin-54024670-Diamond Matt Grey-MATT_BLACK-200 | 200 | Vanity unit 580/475 with 2 drawers for washbasin-54024670-Diamond Matt Grey-MATT_BLACK-200 | Xelu Q Vanity unit Diamond Matt Grey 580/475 with 2 drawers for washbasin | Vanity unit 580/475 with 2 drawers for washbasin-54024670-Diamond Matt Grey-MATT_BLACK-200 | Diamond Matt Grey | 54024XXX | MATT_BLACK | 28.2 |
| Vanity unit 580_475 with 2 drawers for washbasin-54024670-Diamond Matt Grey-MATT_BLACK-400 | 54024670 | Vanity unit 580/475 with 2 drawers for washbasin | 4059625455630 | 580 | Vanity unit 580/475 with 2 drawers for washbasin-54024670-Diamond Matt Grey-MATT_BLACK-400 | 400 | Vanity unit 580/475 with 2 drawers for washbasin-54024670-Diamond Matt Grey-MATT_BLACK-400 | Xelu Q Vanity unit Diamond Matt Grey 580/475 with 2 drawers for washbasin | Vanity unit 580/475 with 2 drawers for washbasin-54024670-Diamond Matt Grey-MATT_BLACK-400 | Diamond Matt Grey | 54024XXX | MATT_BLACK | 28.2 |
| Vanity unit 580_475 with 2 drawers for washbasin-54024700-Diamond Matt Grey-MATT_WHITE-200 | 54024700 | Vanity unit 580/475 with 2 drawers for washbasin | 4059625455630 | 580 | Vanity unit 580/475 with 2 drawers for washbasin-54024700-Diamond Matt Grey-MATT_WHITE-200 | 200 | Vanity unit 580/475 with 2 drawers for washbasin-54024700-Diamond Matt Grey-MATT_WHITE-200 | Xelu Q Vanity unit Diamond Matt Grey 580/475 with 2 drawers for washbasin | Vanity unit 580/475 with 2 drawers for washbasin-54024700-Diamond Matt Grey-MATT_WHITE-200 | Diamond Matt Grey | 54024XXX | MATT_WHITE | 28.2 |
| Vanity unit 580_475 with 2 drawers for washbasin-54024700-Diamond Matt Grey-MATT_WHITE-400 | 54024700 | Vanity unit 580/475 with 2 drawers for washbasin | 4059625455630 | 580 | Vanity unit 580/475 with 2 drawers for washbasin-54024700-Diamond Matt Grey-MATT_WHITE-400 | 400 | Vanity unit 580/475 with 2 drawers for washbasin-54024700-Diamond Matt Grey-MATT_WHITE-400 | Xelu Q Vanity unit Diamond Matt Grey 580/475 with 2 drawers for washbasin | Vanity unit 580/475 with 2 drawers for washbasin-54024700-Diamond Matt Grey-MATT_WHITE-400 | Diamond Matt Grey | 54024XXX | MATT_WHITE | 28.2 |
| Vanity unit 580_475 with 2 drawers for washbasin-54025000-Natural Oak-CHROME-200 | 54025000 | Vanity unit 580/475 with 2 drawers for washbasin | 4059625455609 | 580 | Vanity unit 580/475 with 2 drawers for washbasin-54025000-Natural Oak-CHROME-200 | 200 | Vanity unit 580/475 with 2 drawers for washbasin-54025000-Natural Oak-CHROME-200 | Xelu Q Vanity unit Natural Oak 580/475 with 2 drawers for washbasin | Vanity unit 580/475 with 2 drawers for washbasin-54025000-Natural Oak-CHROME-200 | Natural Oak | 54025XXX | CHROME | 28.2 |
| Vanity unit 580_475 with 2 drawers for washbasin-54025000-Natural Oak-CHROME-400 | 54025000 | Vanity unit 580/475 with 2 drawers for washbasin | 4059625455609 | 580 | Vanity unit 580/475 with 2 drawers for washbasin-54025000-Natural Oak-CHROME-400 | 400 | Vanity unit 580/475 with 2 drawers for washbasin-54025000-Natural Oak-CHROME-400 | Xelu Q Vanity unit Natural Oak 580/475 with 2 drawers for washbasin | Vanity unit 580/475 with 2 drawers for washbasin-54025000-Natural Oak-CHROME-400 | Natural Oak | 54025XXX | CHROME | 28.2 |
| Vanity unit 580_475 with 2 drawers for washbasin-54025670-Natural Oak-MATT_BLACK-200 | 54025670 | Vanity unit 580/475 with 2 drawers for washbasin | 4059625455609 | 580 | Vanity unit 580/475 with 2 drawers for washbasin-54025670-Natural Oak-MATT_BLACK-200 | 200 | Vanity unit 580/475 with 2 drawers for washbasin-54025670-Natural Oak-MATT_BLACK-200 | Xelu Q Vanity unit Natural Oak 580/475 with 2 drawers for washbasin | Vanity unit 580/475 with 2 drawers for washbasin-54025670-Natural Oak-MATT_BLACK-200 | Natural Oak | 54025XXX | MATT_BLACK | 28.2 |
| Vanity unit 580_475 with 2 drawers for washbasin-54025670-Natural Oak-MATT_BLACK-400 | 54025670 | Vanity unit 580/475 with 2 drawers for washbasin | 4059625455609 | 580 | Vanity unit 580/475 with 2 drawers for washbasin-54025670-Natural Oak-MATT_BLACK-400 | 400 | Vanity unit 580/475 with 2 drawers for washbasin-54025670-Natural Oak-MATT_BLACK-400 | Xelu Q Vanity unit Natural Oak 580/475 with 2 drawers for washbasin | Vanity unit 580/475 with 2 drawers for washbasin-54025670-Natural Oak-MATT_BLACK-400 | Natural Oak | 54025XXX | MATT_BLACK | 28.2 |
| Vanity unit 580_475 with 2 drawers for washbasin-54025700-Natural Oak-MATT_WHITE-200 | 54025700 | Vanity unit 580/475 with 2 drawers for washbasin | 4059625455609 | 580 | Vanity unit 580/475 with 2 drawers for washbasin-54025700-Natural Oak-MATT_WHITE-200 | 200 | Vanity unit 580/475 with 2 drawers for washbasin-54025700-Natural Oak-MATT_WHITE-200 | Xelu Q Vanity unit Natural Oak 580/475 with 2 drawers for washbasin | Vanity unit 580/475 with 2 drawers for washbasin-54025700-Natural Oak-MATT_WHITE-200 | Natural Oak | 54025XXX | MATT_WHITE | 28.2 |
| Vanity unit 580_475 with 2 drawers for washbasin-54025700-Natural Oak-MATT_WHITE-400 | 54025700 | Vanity unit 580/475 with 2 drawers for washbasin | 4059625455609 | 580 | Vanity unit 580/475 with 2 drawers for washbasin-54025700-Natural Oak-MATT_WHITE-400 | 400 | Vanity unit 580/475 with 2 drawers for washbasin-54025700-Natural Oak-MATT_WHITE-400 | Xelu Q Vanity unit Natural Oak 580/475 with 2 drawers for washbasin | Vanity unit 580/475 with 2 drawers for washbasin-54025700-Natural Oak-MATT_WHITE-400 | Natural Oak | 54025XXX | MATT_WHITE | 28.2 |
| Vanity unit 580_475 with 2 drawers for washbasin-54026000-Dark Walnut-CHROME-200 | 54026000 | Vanity unit 580/475 with 2 drawers for washbasin | 4059625455579 | 580 | Vanity unit 580/475 with 2 drawers for washbasin-54026000-Dark Walnut-CHROME-200 | 200 | Vanity unit 580/475 with 2 drawers for washbasin-54026000-Dark Walnut-CHROME-200 | Xelu Q Vanity unit Dark Walnut 580/475 with 2 drawers for washbasin | Vanity unit 580/475 with 2 drawers for washbasin-54026000-Dark Walnut-CHROME-200 | Dark Walnut | 54026XXX | CHROME | 28.2 |
| Vanity unit 580_475 with 2 drawers for washbasin-54026000-Dark Walnut-CHROME-400 | 54026000 | Vanity unit 580/475 with 2 drawers for washbasin | 4059625455579 | 580 | Vanity unit 580/475 with 2 drawers for washbasin-54026000-Dark Walnut-CHROME-400 | 400 | Vanity unit 580/475 with 2 drawers for washbasin-54026000-Dark Walnut-CHROME-400 | Xelu Q Vanity unit Dark Walnut 580/475 with 2 drawers for washbasin | Vanity unit 580/475 with 2 drawers for washbasin-54026000-Dark Walnut-CHROME-400 | Dark Walnut | 54026XXX | CHROME | 28.2 |
| Vanity unit 580_475 with 2 drawers for washbasin-54026670-Dark Walnut-MATT_BLACK-200 | 54026670 | Vanity unit 580/475 with 2 drawers for washbasin | 4059625455579 | 580 | Vanity unit 580/475 with 2 drawers for washbasin-54026670-Dark Walnut-MATT_BLACK-200 | 200 | Vanity unit 580/475 with 2 drawers for washbasin-54026670-Dark Walnut-MATT_BLACK-200 | Xelu Q Vanity unit Dark Walnut 580/475 with 2 drawers for washbasin | Vanity unit 580/475 with 2 drawers for washbasin-54026670-Dark Walnut-MATT_BLACK-200 | Dark Walnut | 54026XXX | MATT_BLACK | 28.2 |
| Vanity unit 580_475 with 2 drawers for washbasin-54026670-Dark Walnut-MATT_BLACK-400 | 54026670 | Vanity unit 580/475 with 2 drawers for washbasin | 4059625455579 | 580 | Vanity unit 580/475 with 2 drawers for washbasin-54026670-Dark Walnut-MATT_BLACK-400 | 400 | Vanity unit 580/475 with 2 drawers for washbasin-54026670-Dark Walnut-MATT_BLACK-400 | Xelu Q Vanity unit Dark Walnut 580/475 with 2 drawers for washbasin | Vanity unit 580/475 with 2 drawers for washbasin-54026670-Dark Walnut-MATT_BLACK-400 | Dark Walnut | 54026XXX | MATT_BLACK | 28.2 |
| Vanity unit 580_475 with 2 drawers for washbasin-54026700-Dark Walnut-MATT_WHITE-200 | 54026700 | Vanity unit 580/475 with 2 drawers for washbasin | 4059625455579 | 580 | Vanity unit 580/475 with 2 drawers for washbasin-54026700-Dark Walnut-MATT_WHITE-200 | 200 | Vanity unit 580/475 with 2 drawers for washbasin-54026700-Dark Walnut-MATT_WHITE-200 | Xelu Q Vanity unit Dark Walnut 580/475 with 2 drawers for washbasin | Vanity unit 580/475 with 2 drawers for washbasin-54026700-Dark Walnut-MATT_WHITE-200 | Dark Walnut | 54026XXX | MATT_WHITE | 28.2 |
| Vanity unit 580_475 with 2 drawers for washbasin-54026700-Dark Walnut-MATT_WHITE-400 | 54026700 | Vanity unit 580/475 with 2 drawers for washbasin | 4059625455579 | 580 | Vanity unit 580/475 with 2 drawers for washbasin-54026700-Dark Walnut-MATT_WHITE-400 | 400 | Vanity unit 580/475 with 2 drawers for washbasin-54026700-Dark Walnut-MATT_WHITE-400 | Xelu Q Vanity unit Dark Walnut 580/475 with 2 drawers for washbasin | Vanity unit 580/475 with 2 drawers for washbasin-54026700-Dark Walnut-MATT_WHITE-400 | Dark Walnut | 54026XXX | MATT_WHITE | 28.2 |
| Vanity unit 780_475 with 2 drawers for washbasin-54027000-High Gloss White-CHROME-200 | 54027000 | Vanity unit 780/475 with 2 drawers for washbasin | 4059625455548 | 780 | Vanity unit 780/475 with 2 drawers for washbasin-54027000-High Gloss White-CHROME-200 | 200 | Vanity unit 780/475 with 2 drawers for washbasin-54027000-High Gloss White-CHROME-200 | Xelu Q Vanity unit High Gloss White 780/475 with 2 drawers for washbasin | Vanity unit 780/475 with 2 drawers for washbasin-54027000-High Gloss White-CHROME-200 | High Gloss White | 54027XXX | CHROME | 33.3 |
| Vanity unit 780_475 with 2 drawers for washbasin-54027000-High Gloss White-CHROME-400 | 54027000 | Vanity unit 780/475 with 2 drawers for washbasin | 4059625455548 | 780 | Vanity unit 780/475 with 2 drawers for washbasin-54027000-High Gloss White-CHROME-400 | 400 | Vanity unit 780/475 with 2 drawers for washbasin-54027000-High Gloss White-CHROME-400 | Xelu Q Vanity unit High Gloss White 780/475 with 2 drawers for washbasin | Vanity unit 780/475 with 2 drawers for washbasin-54027000-High Gloss White-CHROME-400 | High Gloss White | 54027XXX | CHROME | 33.3 |
| Vanity unit 780_475 with 2 drawers for washbasin-54027670-High Gloss White-MATT_BLACK-200 | 54027670 | Vanity unit 780/475 with 2 drawers for washbasin | 4059625455548 | 780 | Vanity unit 780/475 with 2 drawers for washbasin-54027670-High Gloss White-MATT_BLACK-200 | 200 | Vanity unit 780/475 with 2 drawers for washbasin-54027670-High Gloss White-MATT_BLACK-200 | Xelu Q Vanity unit High Gloss White 780/475 with 2 drawers for washbasin | Vanity unit 780/475 with 2 drawers for washbasin-54027670-High Gloss White-MATT_BLACK-200 | High Gloss White | 54027XXX | MATT_BLACK | 33.3 |
| Vanity unit 780_475 with 2 drawers for washbasin-54027670-High Gloss White-MATT_BLACK-400 | 54027670 | Vanity unit 780/475 with 2 drawers for washbasin | 4059625455548 | 780 | Vanity unit 780/475 with 2 drawers for washbasin-54027670-High Gloss White-MATT_BLACK-400 | 400 | Vanity unit 780/475 with 2 drawers for washbasin-54027670-High Gloss White-MATT_BLACK-400 | Xelu Q Vanity unit High Gloss White 780/475 with 2 drawers for washbasin | Vanity unit 780/475 with 2 drawers for washbasin-54027670-High Gloss White-MATT_BLACK-400 | High Gloss White | 54027XXX | MATT_BLACK | 33.3 |
| Vanity unit 780_475 with 2 drawers for washbasin-54027700-High Gloss White-MATT_WHITE-200 | 54027700 | Vanity unit 780/475 with 2 drawers for washbasin | 4059625455548 | 780 | Vanity unit 780/475 with 2 drawers for washbasin-54027700-High Gloss White-MATT_WHITE-200 | 200 | Vanity unit 780/475 with 2 drawers for washbasin-54027700-High Gloss White-MATT_WHITE-200 | Xelu Q Vanity unit High Gloss White 780/475 with 2 drawers for washbasin | Vanity unit 780/475 with 2 drawers for washbasin-54027700-High Gloss White-MATT_WHITE-200 | High Gloss White | 54027XXX | MATT_WHITE | 33.3 |
| Vanity unit 780_475 with 2 drawers for washbasin-54027700-High Gloss White-MATT_WHITE-400 | 54027700 | Vanity unit 780/475 with 2 drawers for washbasin | 4059625455548 | 780 | Vanity unit 780/475 with 2 drawers for washbasin-54027700-High Gloss White-MATT_WHITE-400 | 400 | Vanity unit 780/475 with 2 drawers for washbasin-54027700-High Gloss White-MATT_WHITE-400 | Xelu Q Vanity unit High Gloss White 780/475 with 2 drawers for washbasin | Vanity unit 780/475 with 2 drawers for washbasin-54027700-High Gloss White-MATT_WHITE-400 | High Gloss White | 54027XXX | MATT_WHITE | 33.3 |
| Vanity unit 780_475 with 2 drawers for washbasin-54028000-Diamond Matt Grey-CHROME-200 | 54028000 | Vanity unit 780/475 with 2 drawers for washbasin | 4059625455517 | 780 | Vanity unit 780/475 with 2 drawers for washbasin-54028000-Diamond Matt Grey-CHROME-200 | 200 | Vanity unit 780/475 with 2 drawers for washbasin-54028000-Diamond Matt Grey-CHROME-200 | Xelu Q Vanity unit Diamond Matt Grey 780/475 with 2 drawers for washbasin | Vanity unit 780/475 with 2 drawers for washbasin-54028000-Diamond Matt Grey-CHROME-200 | Diamond Matt Grey | 54028XXX | CHROME | 33.3 |
| Vanity unit 780_475 with 2 drawers for washbasin-54028000-Diamond Matt Grey-CHROME-400 | 54028000 | Vanity unit 780/475 with 2 drawers for washbasin | 4059625455517 | 780 | Vanity unit 780/475 with 2 drawers for washbasin-54028000-Diamond Matt Grey-CHROME-400 | 400 | Vanity unit 780/475 with 2 drawers for washbasin-54028000-Diamond Matt Grey-CHROME-400 | Xelu Q Vanity unit Diamond Matt Grey 780/475 with 2 drawers for washbasin | Vanity unit 780/475 with 2 drawers for washbasin-54028000-Diamond Matt Grey-CHROME-400 | Diamond Matt Grey | 54028XXX | CHROME | 33.3 |
| Vanity unit 780_475 with 2 drawers for washbasin-54028670-Diamond Matt Grey-MATT_BLACK-200 | 54028670 | Vanity unit 780/475 with 2 drawers for washbasin | 4059625455517 | 780 | Vanity unit 780/475 with 2 drawers for washbasin-54028670-Diamond Matt Grey-MATT_BLACK-200 | 200 | Vanity unit 780/475 with 2 drawers for washbasin-54028670-Diamond Matt Grey-MATT_BLACK-200 | Xelu Q Vanity unit Diamond Matt Grey 780/475 with 2 drawers for washbasin | Vanity unit 780/475 with 2 drawers for washbasin-54028670-Diamond Matt Grey-MATT_BLACK-200 | Diamond Matt Grey | 54028XXX | MATT_BLACK | 33.3 |
| Vanity unit 780_475 with 2 drawers for washbasin-54028670-Diamond Matt Grey-MATT_BLACK-400 | 54028670 | Vanity unit 780/475 with 2 drawers for washbasin | 4059625455517 | 780 | Vanity unit 780/475 with 2 drawers for washbasin-54028670-Diamond Matt Grey-MATT_BLACK-400 | 400 | Vanity unit 780/475 with 2 drawers for washbasin-54028670-Diamond Matt Grey-MATT_BLACK-400 | Xelu Q Vanity unit Diamond Matt Grey 780/475 with 2 drawers for washbasin | Vanity unit 780/475 with 2 drawers for washbasin-54028670-Diamond Matt Grey-MATT_BLACK-400 | Diamond Matt Grey | 54028XXX | MATT_BLACK | 33.3 |
| Vanity unit 780_475 with 2 drawers for washbasin-54028700-Diamond Matt Grey-MATT_WHITE-200 | 54028700 | Vanity unit 780/475 with 2 drawers for washbasin | 4059625455517 | 780 | Vanity unit 780/475 with 2 drawers for washbasin-54028700-Diamond Matt Grey-MATT_WHITE-200 | 200 | Vanity unit 780/475 with 2 drawers for washbasin-54028700-Diamond Matt Grey-MATT_WHITE-200 | Xelu Q Vanity unit Diamond Matt Grey 780/475 with 2 drawers for washbasin | Vanity unit 780/475 with 2 drawers for washbasin-54028700-Diamond Matt Grey-MATT_WHITE-200 | Diamond Matt Grey | 54028XXX | MATT_WHITE | 33.3 |
| Vanity unit 780_475 with 2 drawers for washbasin-54028700-Diamond Matt Grey-MATT_WHITE-400 | 54028700 | Vanity unit 780/475 with 2 drawers for washbasin | 4059625455517 | 780 | Vanity unit 780/475 with 2 drawers for washbasin-54028700-Diamond Matt Grey-MATT_WHITE-400 | 400 | Vanity unit 780/475 with 2 drawers for washbasin-54028700-Diamond Matt Grey-MATT_WHITE-400 | Xelu Q Vanity unit Diamond Matt Grey 780/475 with 2 drawers for washbasin | Vanity unit 780/475 with 2 drawers for washbasin-54028700-Diamond Matt Grey-MATT_WHITE-400 | Diamond Matt Grey | 54028XXX | MATT_WHITE | 33.3 |
| Vanity unit 780_475 with 2 drawers for washbasin-54029000-Natural Oak-CHROME-200 | 54029000 | Vanity unit 780/475 with 2 drawers for washbasin | 4059625455487 | 780 | Vanity unit 780/475 with 2 drawers for washbasin-54029000-Natural Oak-CHROME-200 | 200 | Vanity unit 780/475 with 2 drawers for washbasin-54029000-Natural Oak-CHROME-200 | Xelu Q Vanity unit Natural Oak 780/475 with 2 drawers for washbasin | Vanity unit 780/475 with 2 drawers for washbasin-54029000-Natural Oak-CHROME-200 | Natural Oak | 54029XXX | CHROME | 33.3 |
| Vanity unit 780_475 with 2 drawers for washbasin-54029000-Natural Oak-CHROME-400 | 54029000 | Vanity unit 780/475 with 2 drawers for washbasin | 4059625455487 | 780 | Vanity unit 780/475 with 2 drawers for washbasin-54029000-Natural Oak-CHROME-400 | 400 | Vanity unit 780/475 with 2 drawers for washbasin-54029000-Natural Oak-CHROME-400 | Xelu Q Vanity unit Natural Oak 780/475 with 2 drawers for washbasin | Vanity unit 780/475 with 2 drawers for washbasin-54029000-Natural Oak-CHROME-400 | Natural Oak | 54029XXX | CHROME | 33.3 |
| Vanity unit 780_475 with 2 drawers for washbasin-54029670-Natural Oak-MATT_BLACK-200 | 54029670 | Vanity unit 780/475 with 2 drawers for washbasin | 4059625455487 | 780 | Vanity unit 780/475 with 2 drawers for washbasin-54029670-Natural Oak-MATT_BLACK-200 | 200 | Vanity unit 780/475 with 2 drawers for washbasin-54029670-Natural Oak-MATT_BLACK-200 | Xelu Q Vanity unit Natural Oak 780/475 with 2 drawers for washbasin | Vanity unit 780/475 with 2 drawers for washbasin-54029670-Natural Oak-MATT_BLACK-200 | Natural Oak | 54029XXX | MATT_BLACK | 33.3 |
| Vanity unit 780_475 with 2 drawers for washbasin-54029670-Natural Oak-MATT_BLACK-400 | 54029670 | Vanity unit 780/475 with 2 drawers for washbasin | 4059625455487 | 780 | Vanity unit 780/475 with 2 drawers for washbasin-54029670-Natural Oak-MATT_BLACK-400 | 400 | Vanity unit 780/475 with 2 drawers for washbasin-54029670-Natural Oak-MATT_BLACK-400 | Xelu Q Vanity unit Natural Oak 780/475 with 2 drawers for washbasin | Vanity unit 780/475 with 2 drawers for washbasin-54029670-Natural Oak-MATT_BLACK-400 | Natural Oak | 54029XXX | MATT_BLACK | 33.3 |
| Vanity unit 780_475 with 2 drawers for washbasin-54029700-Natural Oak-MATT_WHITE-200 | 54029700 | Vanity unit 780/475 with 2 drawers for washbasin | 4059625455487 | 780 | Vanity unit 780/475 with 2 drawers for washbasin-54029700-Natural Oak-MATT_WHITE-200 | 200 | Vanity unit 780/475 with 2 drawers for washbasin-54029700-Natural Oak-MATT_WHITE-200 | Xelu Q Vanity unit Natural Oak 780/475 with 2 drawers for washbasin | Vanity unit 780/475 with 2 drawers for washbasin-54029700-Natural Oak-MATT_WHITE-200 | Natural Oak | 54029XXX | MATT_WHITE | 33.3 |
| Vanity unit 780_475 with 2 drawers for washbasin-54029700-Natural Oak-MATT_WHITE-400 | 54029700 | Vanity unit 780/475 with 2 drawers for washbasin | 4059625455487 | 780 | Vanity unit 780/475 with 2 drawers for washbasin-54029700-Natural Oak-MATT_WHITE-400 | 400 | Vanity unit 780/475 with 2 drawers for washbasin-54029700-Natural Oak-MATT_WHITE-400 | Xelu Q Vanity unit Natural Oak 780/475 with 2 drawers for washbasin | Vanity unit 780/475 with 2 drawers for washbasin-54029700-Natural Oak-MATT_WHITE-400 | Natural Oak | 54029XXX | MATT_WHITE | 33.3 |
| Vanity unit 780_475 with 2 drawers for washbasin-54030000-Dark Walnut-CHROME-200 | 54030000 | Vanity unit 780/475 with 2 drawers for washbasin | 4059625455456 | 780 | Vanity unit 780/475 with 2 drawers for washbasin-54030000-Dark Walnut-CHROME-200 | 200 | Vanity unit 780/475 with 2 drawers for washbasin-54030000-Dark Walnut-CHROME-200 | Xelu Q Vanity unit Dark Walnut 780/475 with 2 drawers for washbasin | Vanity unit 780/475 with 2 drawers for washbasin-54030000-Dark Walnut-CHROME-200 | Dark Walnut | 54030XXX | CHROME | 33.3 |
| Vanity unit 780_475 with 2 drawers for washbasin-54030000-Dark Walnut-CHROME-400 | 54030000 | Vanity unit 780/475 with 2 drawers for washbasin | 4059625455456 | 780 | Vanity unit 780/475 with 2 drawers for washbasin-54030000-Dark Walnut-CHROME-400 | 400 | Vanity unit 780/475 with 2 drawers for washbasin-54030000-Dark Walnut-CHROME-400 | Xelu Q Vanity unit Dark Walnut 780/475 with 2 drawers for washbasin | Vanity unit 780/475 with 2 drawers for washbasin-54030000-Dark Walnut-CHROME-400 | Dark Walnut | 54030XXX | CHROME | 33.3 |
| Vanity unit 780_475 with 2 drawers for washbasin-54030670-Dark Walnut-MATT_BLACK-200 | 54030670 | Vanity unit 780/475 with 2 drawers for washbasin | 4059625455456 | 780 | Vanity unit 780/475 with 2 drawers for washbasin-54030670-Dark Walnut-MATT_BLACK-200 | 200 | Vanity unit 780/475 with 2 drawers for washbasin-54030670-Dark Walnut-MATT_BLACK-200 | Xelu Q Vanity unit Dark Walnut 780/475 with 2 drawers for washbasin | Vanity unit 780/475 with 2 drawers for washbasin-54030670-Dark Walnut-MATT_BLACK-200 | Dark Walnut | 54030XXX | MATT_BLACK | 33.3 |
| Vanity unit 780_475 with 2 drawers for washbasin-54030670-Dark Walnut-MATT_BLACK-400 | 54030670 | Vanity unit 780/475 with 2 drawers for washbasin | 4059625455456 | 780 | Vanity unit 780/475 with 2 drawers for washbasin-54030670-Dark Walnut-MATT_BLACK-400 | 400 | Vanity unit 780/475 with 2 drawers for washbasin-54030670-Dark Walnut-MATT_BLACK-400 | Xelu Q Vanity unit Dark Walnut 780/475 with 2 drawers for washbasin | Vanity unit 780/475 with 2 drawers for washbasin-54030670-Dark Walnut-MATT_BLACK-400 | Dark Walnut | 54030XXX | MATT_BLACK | 33.3 |
| Vanity unit 780_475 with 2 drawers for washbasin-54030700-Dark Walnut-MATT_WHITE-200 | 54030700 | Vanity unit 780/475 with 2 drawers for washbasin | 4059625455456 | 780 | Vanity unit 780/475 with 2 drawers for washbasin-54030700-Dark Walnut-MATT_WHITE-200 | 200 | Vanity unit 780/475 with 2 drawers for washbasin-54030700-Dark Walnut-MATT_WHITE-200 | Xelu Q Vanity unit Dark Walnut 780/475 with 2 drawers for washbasin | Vanity unit 780/475 with 2 drawers for washbasin-54030700-Dark Walnut-MATT_WHITE-200 | Dark Walnut | 54030XXX | MATT_WHITE | 33.3 |
| Vanity unit 780_475 with 2 drawers for washbasin-54030700-Dark Walnut-MATT_WHITE-400 | 54030700 | Vanity unit 780/475 with 2 drawers for washbasin | 4059625455456 | 780 | Vanity unit 780/475 with 2 drawers for washbasin-54030700-Dark Walnut-MATT_WHITE-400 | 400 | Vanity unit 780/475 with 2 drawers for washbasin-54030700-Dark Walnut-MATT_WHITE-400 | Xelu Q Vanity unit Dark Walnut 780/475 with 2 drawers for washbasin | Vanity unit 780/475 with 2 drawers for washbasin-54030700-Dark Walnut-MATT_WHITE-400 | Dark Walnut | 54030XXX | MATT_WHITE | 33.3 |
| Vanity unit 980_475 with 2 drawers for washbasin-54031000-High Gloss White-CHROME-200 | 54031000 | Vanity unit 980/475 with 2 drawers for washbasin | 4059625455425 | 980 | Vanity unit 980/475 with 2 drawers for washbasin-54031000-High Gloss White-CHROME-200 | 200 | Vanity unit 980/475 with 2 drawers for washbasin-54031000-High Gloss White-CHROME-200 | Xelu Q Vanity unit High Gloss White 980/475 with 2 drawers for washbasin | Vanity unit 980/475 with 2 drawers for washbasin-54031000-High Gloss White-CHROME-200 | High Gloss White | 54031XXX | CHROME | 39.8 |
| Vanity unit 980_475 with 2 drawers for washbasin-54031000-High Gloss White-CHROME-400 | 54031000 | Vanity unit 980/475 with 2 drawers for washbasin | 4059625455425 | 980 | Vanity unit 980/475 with 2 drawers for washbasin-54031000-High Gloss White-CHROME-400 | 400 | Vanity unit 980/475 with 2 drawers for washbasin-54031000-High Gloss White-CHROME-400 | Xelu Q Vanity unit High Gloss White 980/475 with 2 drawers for washbasin | Vanity unit 980/475 with 2 drawers for washbasin-54031000-High Gloss White-CHROME-400 | High Gloss White | 54031XXX | CHROME | 39.8 |
| Vanity unit 980_475 with 2 drawers for washbasin-54031670-High Gloss White-MATT_BLACK-200 | 54031670 | Vanity unit 980/475 with 2 drawers for washbasin | 4059625455425 | 980 | Vanity unit 980/475 with 2 drawers for washbasin-54031670-High Gloss White-MATT_BLACK-200 | 200 | Vanity unit 980/475 with 2 drawers for washbasin-54031670-High Gloss White-MATT_BLACK-200 | Xelu Q Vanity unit High Gloss White 980/475 with 2 drawers for washbasin | Vanity unit 980/475 with 2 drawers for washbasin-54031670-High Gloss White-MATT_BLACK-200 | High Gloss White | 54031XXX | MATT_BLACK | 39.8 |
| Vanity unit 980_475 with 2 drawers for washbasin-54031670-High Gloss White-MATT_BLACK-400 | 54031670 | Vanity unit 980/475 with 2 drawers for washbasin | 4059625455425 | 980 | Vanity unit 980/475 with 2 drawers for washbasin-54031670-High Gloss White-MATT_BLACK-400 | 400 | Vanity unit 980/475 with 2 drawers for washbasin-54031670-High Gloss White-MATT_BLACK-400 | Xelu Q Vanity unit High Gloss White 980/475 with 2 drawers for washbasin | Vanity unit 980/475 with 2 drawers for washbasin-54031670-High Gloss White-MATT_BLACK-400 | High Gloss White | 54031XXX | MATT_BLACK | 39.8 |
| Vanity unit 980_475 with 2 drawers for washbasin-54031700-High Gloss White-MATT_WHITE-200 | 54031700 | Vanity unit 980/475 with 2 drawers for washbasin | 4059625455425 | 980 | Vanity unit 980/475 with 2 drawers for washbasin-54031700-High Gloss White-MATT_WHITE-200 | 200 | Vanity unit 980/475 with 2 drawers for washbasin-54031700-High Gloss White-MATT_WHITE-200 | Xelu Q Vanity unit High Gloss White 980/475 with 2 drawers for washbasin | Vanity unit 980/475 with 2 drawers for washbasin-54031700-High Gloss White-MATT_WHITE-200 | High Gloss White | 54031XXX | MATT_WHITE | 39.8 |
| Vanity unit 980_475 with 2 drawers for washbasin-54031700-High Gloss White-MATT_WHITE-400 | 54031700 | Vanity unit 980/475 with 2 drawers for washbasin | 4059625455425 | 980 | Vanity unit 980/475 with 2 drawers for washbasin-54031700-High Gloss White-MATT_WHITE-400 | 400 | Vanity unit 980/475 with 2 drawers for washbasin-54031700-High Gloss White-MATT_WHITE-400 | Xelu Q Vanity unit High Gloss White 980/475 with 2 drawers for washbasin | Vanity unit 980/475 with 2 drawers for washbasin-54031700-High Gloss White-MATT_WHITE-400 | High Gloss White | 54031XXX | MATT_WHITE | 39.8 |
| Vanity unit 980_475 with 2 drawers for washbasin-54032000-Diamond Matt Grey-CHROME-200 | 54032000 | Vanity unit 980/475 with 2 drawers for washbasin | 4059625455395 | 980 | Vanity unit 980/475 with 2 drawers for washbasin-54032000-Diamond Matt Grey-CHROME-200 | 200 | Vanity unit 980/475 with 2 drawers for washbasin-54032000-Diamond Matt Grey-CHROME-200 | Xelu Q Vanity unit Diamond Matt Grey 980/475 with 2 drawers for washbasin | Vanity unit 980/475 with 2 drawers for washbasin-54032000-Diamond Matt Grey-CHROME-200 | Diamond Matt Grey | 54032XXX | CHROME | 39.8 |
| Vanity unit 980_475 with 2 drawers for washbasin-54032000-Diamond Matt Grey-CHROME-400 | 54032000 | Vanity unit 980/475 with 2 drawers for washbasin | 4059625455395 | 980 | Vanity unit 980/475 with 2 drawers for washbasin-54032000-Diamond Matt Grey-CHROME-400 | 400 | Vanity unit 980/475 with 2 drawers for washbasin-54032000-Diamond Matt Grey-CHROME-400 | Xelu Q Vanity unit Diamond Matt Grey 980/475 with 2 drawers for washbasin | Vanity unit 980/475 with 2 drawers for washbasin-54032000-Diamond Matt Grey-CHROME-400 | Diamond Matt Grey | 54032XXX | CHROME | 39.8 |
| Vanity unit 980_475 with 2 drawers for washbasin-54032670-Diamond Matt Grey-MATT_BLACK-200 | 54032670 | Vanity unit 980/475 with 2 drawers for washbasin | 4059625455395 | 980 | Vanity unit 980/475 with 2 drawers for washbasin-54032670-Diamond Matt Grey-MATT_BLACK-200 | 200 | Vanity unit 980/475 with 2 drawers for washbasin-54032670-Diamond Matt Grey-MATT_BLACK-200 | Xelu Q Vanity unit Diamond Matt Grey 980/475 with 2 drawers for washbasin | Vanity unit 980/475 with 2 drawers for washbasin-54032670-Diamond Matt Grey-MATT_BLACK-200 | Diamond Matt Grey | 54032XXX | MATT_BLACK | 39.8 |
| Vanity unit 980_475 with 2 drawers for washbasin-54032670-Diamond Matt Grey-MATT_BLACK-400 | 54032670 | Vanity unit 980/475 with 2 drawers for washbasin | 4059625455395 | 980 | Vanity unit 980/475 with 2 drawers for washbasin-54032670-Diamond Matt Grey-MATT_BLACK-400 | 400 | Vanity unit 980/475 with 2 drawers for washbasin-54032670-Diamond Matt Grey-MATT_BLACK-400 | Xelu Q Vanity unit Diamond Matt Grey 980/475 with 2 drawers for washbasin | Vanity unit 980/475 with 2 drawers for washbasin-54032670-Diamond Matt Grey-MATT_BLACK-400 | Diamond Matt Grey | 54032XXX | MATT_BLACK | 39.8 |
| Vanity unit 980_475 with 2 drawers for washbasin-54032700-Diamond Matt Grey-MATT_WHITE-200 | 54032700 | Vanity unit 980/475 with 2 drawers for washbasin | 4059625455395 | 980 | Vanity unit 980/475 with 2 drawers for washbasin-54032700-Diamond Matt Grey-MATT_WHITE-200 | 200 | Vanity unit 980/475 with 2 drawers for washbasin-54032700-Diamond Matt Grey-MATT_WHITE-200 | Xelu Q Vanity unit Diamond Matt Grey 980/475 with 2 drawers for washbasin | Vanity unit 980/475 with 2 drawers for washbasin-54032700-Diamond Matt Grey-MATT_WHITE-200 | Diamond Matt Grey | 54032XXX | MATT_WHITE | 39.8 |
| Vanity unit 980_475 with 2 drawers for washbasin-54032700-Diamond Matt Grey-MATT_WHITE-400 | 54032700 | Vanity unit 980/475 with 2 drawers for washbasin | 4059625455395 | 980 | Vanity unit 980/475 with 2 drawers for washbasin-54032700-Diamond Matt Grey-MATT_WHITE-400 | 400 | Vanity unit 980/475 with 2 drawers for washbasin-54032700-Diamond Matt Grey-MATT_WHITE-400 | Xelu Q Vanity unit Diamond Matt Grey 980/475 with 2 drawers for washbasin | Vanity unit 980/475 with 2 drawers for washbasin-54032700-Diamond Matt Grey-MATT_WHITE-400 | Diamond Matt Grey | 54032XXX | MATT_WHITE | 39.8 |
| Vanity unit 980_475 with 2 drawers for washbasin-54033000-Natural Oak-CHROME-200 | 54033000 | Vanity unit 980/475 with 2 drawers for washbasin | 4059625455364 | 980 | Vanity unit 980/475 with 2 drawers for washbasin-54033000-Natural Oak-CHROME-200 | 200 | Vanity unit 980/475 with 2 drawers for washbasin-54033000-Natural Oak-CHROME-200 | Xelu Q Vanity unit Natural Oak 980/475 with 2 drawers for washbasin | Vanity unit 980/475 with 2 drawers for washbasin-54033000-Natural Oak-CHROME-200 | Natural Oak | 54033XXX | CHROME | 39.8 |
| Vanity unit 980_475 with 2 drawers for washbasin-54033000-Natural Oak-CHROME-400 | 54033000 | Vanity unit 980/475 with 2 drawers for washbasin | 4059625455364 | 980 | Vanity unit 980/475 with 2 drawers for washbasin-54033000-Natural Oak-CHROME-400 | 400 | Vanity unit 980/475 with 2 drawers for washbasin-54033000-Natural Oak-CHROME-400 | Xelu Q Vanity unit Natural Oak 980/475 with 2 drawers for washbasin | Vanity unit 980/475 with 2 drawers for washbasin-54033000-Natural Oak-CHROME-400 | Natural Oak | 54033XXX | CHROME | 39.8 |
| Vanity unit 980_475 with 2 drawers for washbasin-54033670-Natural Oak-MATT_BLACK-200 | 54033670 | Vanity unit 980/475 with 2 drawers for washbasin | 4059625455364 | 980 | Vanity unit 980/475 with 2 drawers for washbasin-54033670-Natural Oak-MATT_BLACK-200 | 200 | Vanity unit 980/475 with 2 drawers for washbasin-54033670-Natural Oak-MATT_BLACK-200 | Xelu Q Vanity unit Natural Oak 980/475 with 2 drawers for washbasin | Vanity unit 980/475 with 2 drawers for washbasin-54033670-Natural Oak-MATT_BLACK-200 | Natural Oak | 54033XXX | MATT_BLACK | 39.8 |
| Vanity unit 980_475 with 2 drawers for washbasin-54033670-Natural Oak-MATT_BLACK-400 | 54033670 | Vanity unit 980/475 with 2 drawers for washbasin | 4059625455364 | 980 | Vanity unit 980/475 with 2 drawers for washbasin-54033670-Natural Oak-MATT_BLACK-400 | 400 | Vanity unit 980/475 with 2 drawers for washbasin-54033670-Natural Oak-MATT_BLACK-400 | Xelu Q Vanity unit Natural Oak 980/475 with 2 drawers for washbasin | Vanity unit 980/475 with 2 drawers for washbasin-54033670-Natural Oak-MATT_BLACK-400 | Natural Oak | 54033XXX | MATT_BLACK | 39.8 |
| Vanity unit 980_475 with 2 drawers for washbasin-54033700-Natural Oak-MATT_WHITE-200 | 54033700 | Vanity unit 980/475 with 2 drawers for washbasin | 4059625455364 | 980 | Vanity unit 980/475 with 2 drawers for washbasin-54033700-Natural Oak-MATT_WHITE-200 | 200 | Vanity unit 980/475 with 2 drawers for washbasin-54033700-Natural Oak-MATT_WHITE-200 | Xelu Q Vanity unit Natural Oak 980/475 with 2 drawers for washbasin | Vanity unit 980/475 with 2 drawers for washbasin-54033700-Natural Oak-MATT_WHITE-200 | Natural Oak | 54033XXX | MATT_WHITE | 39.8 |
| Vanity unit 980_475 with 2 drawers for washbasin-54033700-Natural Oak-MATT_WHITE-400 | 54033700 | Vanity unit 980/475 with 2 drawers for washbasin | 4059625455364 | 980 | Vanity unit 980/475 with 2 drawers for washbasin-54033700-Natural Oak-MATT_WHITE-400 | 400 | Vanity unit 980/475 with 2 drawers for washbasin-54033700-Natural Oak-MATT_WHITE-400 | Xelu Q Vanity unit Natural Oak 980/475 with 2 drawers for washbasin | Vanity unit 980/475 with 2 drawers for washbasin-54033700-Natural Oak-MATT_WHITE-400 | Natural Oak | 54033XXX | MATT_WHITE | 39.8 |
| Vanity unit 980_475 with 2 drawers for washbasin-54034000-Dark Walnut-CHROME-200 | 54034000 | Vanity unit 980/475 with 2 drawers for washbasin | 4059625455838 | 980 | Vanity unit 980/475 with 2 drawers for washbasin-54034000-Dark Walnut-CHROME-200 | 200 | Vanity unit 980/475 with 2 drawers for washbasin-54034000-Dark Walnut-CHROME-200 | Xelu Q Vanity unit Dark Walnut 980/475 with 2 drawers for washbasin | Vanity unit 980/475 with 2 drawers for washbasin-54034000-Dark Walnut-CHROME-200 | Dark Walnut | 54034XXX | CHROME | 39.8 |
| Vanity unit 980_475 with 2 drawers for washbasin-54034000-Dark Walnut-CHROME-400 | 54034000 | Vanity unit 980/475 with 2 drawers for washbasin | 4059625455838 | 980 | Vanity unit 980/475 with 2 drawers for washbasin-54034000-Dark Walnut-CHROME-400 | 400 | Vanity unit 980/475 with 2 drawers for washbasin-54034000-Dark Walnut-CHROME-400 | Xelu Q Vanity unit Dark Walnut 980/475 with 2 drawers for washbasin | Vanity unit 980/475 with 2 drawers for washbasin-54034000-Dark Walnut-CHROME-400 | Dark Walnut | 54034XXX | CHROME | 39.8 |
| Vanity unit 980_475 with 2 drawers for washbasin-54034670-Dark Walnut-MATT_BLACK-200 | 54034670 | Vanity unit 980/475 with 2 drawers for washbasin | 4059625455838 | 980 | Vanity unit 980/475 with 2 drawers for washbasin-54034670-Dark Walnut-MATT_BLACK-200 | 200 | Vanity unit 980/475 with 2 drawers for washbasin-54034670-Dark Walnut-MATT_BLACK-200 | Xelu Q Vanity unit Dark Walnut 980/475 with 2 drawers for washbasin | Vanity unit 980/475 with 2 drawers for washbasin-54034670-Dark Walnut-MATT_BLACK-200 | Dark Walnut | 54034XXX | MATT_BLACK | 39.8 |
| Vanity unit 980_475 with 2 drawers for washbasin-54034670-Dark Walnut-MATT_BLACK-400 | 54034670 | Vanity unit 980/475 with 2 drawers for washbasin | 4059625455838 | 980 | Vanity unit 980/475 with 2 drawers for washbasin-54034670-Dark Walnut-MATT_BLACK-400 | 400 | Vanity unit 980/475 with 2 drawers for washbasin-54034670-Dark Walnut-MATT_BLACK-400 | Xelu Q Vanity unit Dark Walnut 980/475 with 2 drawers for washbasin | Vanity unit 980/475 with 2 drawers for washbasin-54034670-Dark Walnut-MATT_BLACK-400 | Dark Walnut | 54034XXX | MATT_BLACK | 39.8 |
| Vanity unit 980_475 with 2 drawers for washbasin-54034700-Dark Walnut-MATT_WHITE-200 | 54034700 | Vanity unit 980/475 with 2 drawers for washbasin | 4059625455838 | 980 | Vanity unit 980/475 with 2 drawers for washbasin-54034700-Dark Walnut-MATT_WHITE-200 | 200 | Vanity unit 980/475 with 2 drawers for washbasin-54034700-Dark Walnut-MATT_WHITE-200 | Xelu Q Vanity unit Dark Walnut 980/475 with 2 drawers for washbasin | Vanity unit 980/475 with 2 drawers for washbasin-54034700-Dark Walnut-MATT_WHITE-200 | Dark Walnut | 54034XXX | MATT_WHITE | 39.8 |
| Vanity unit 980_475 with 2 drawers for washbasin-54034700-Dark Walnut-MATT_WHITE-400 | 54034700 | Vanity unit 980/475 with 2 drawers for washbasin | 4059625455838 | 980 | Vanity unit 980/475 with 2 drawers for washbasin-54034700-Dark Walnut-MATT_WHITE-400 | 400 | Vanity unit 980/475 with 2 drawers for washbasin-54034700-Dark Walnut-MATT_WHITE-400 | Xelu Q Vanity unit Dark Walnut 980/475 with 2 drawers for washbasin | Vanity unit 980/475 with 2 drawers for washbasin-54034700-Dark Walnut-MATT_WHITE-400 | Dark Walnut | 54034XXX | MATT_WHITE | 39.8 |

type visibility flags: 120 boolean params named "<type name>_RX0RY0RZ0TX0TY0TZ0_V" — each type sets only its own to Yes (folded from table)

## geometry (parser evidence)
native form markers: Sweep x96
no freeform markers — native parametric forms only
